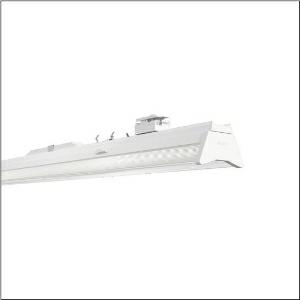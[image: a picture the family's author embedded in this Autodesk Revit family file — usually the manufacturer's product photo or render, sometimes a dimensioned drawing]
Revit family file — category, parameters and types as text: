
# Revit family: licross_r__11_performance_ho_51td16dn4fxm_21ba
name_source: partatom
category: Lighting Fixtures
units: mm (PartAtom-declared; Revit-internal decimal feet)

## family parameters
Cut with Voids When Loaded = No
Host = Face
Light Source = No
Part Type = Normal
Room Calculation Point = No
Round Connector Dimension = Use Diameter
Shared = No

## types (1)
- --- (1 x LED, 15460 lm, 87.3 W, 4000K)
    Apparent Load = 87 VA
    CIE Flux Codes = 63 87 95 78 100
    Color Rendering = 80
    Color Temperature = 4000K
    Default Elevation = 1800 mm
    Description = Licross® 11 Performance HO, luminaire insert, of sheet steel, galvanised, coil coated, white, length: 1.500mm, width: 120mm, height: 123mm, LED rated luminous flux: 15.460lm, light colour: 840, control gear: DALI 2, with plug, 5-pole, with phase selection, mains connection: 220..240V, AC, 50/60Hz, rated input power: 87W, internal wiring halogen-free, primary light control with lens, of plastic, primary optical cover: cover, of PMMA, light emission: direct/indirect distribution, primary light characteristic: symmetric, protection rating (complete): IP54, insulation class (complete): insulation class I (protective earthing), certification: CE, ENEC, VDE, UKCA, protection symbol: D if used in an environment with non-conductive dust loads with corresponding accessories, impact resistance: IK06, permissible ambient temperature for indoor applications: -25..+30°C, corresponds to IFS (International Featured Standards) requirements for safety and quality in the food industry, reducing of maximum allowable ambient temperature of 5°C with ceiling mounting, LABS conformity tested according to VDMA 24364:2018-05, packaging unit: 1 piece
    Height = 114 mm
    Lamp = 1 x LED
    Lamp Light Flux = 15460 lm
    Lamp Power = 87.3 W
    Lamp count = 1
    Length = 1500 mm
    Luminous efficacy = 177 lm/W
    Manufacturer = Siteco
    ModVariant = No
    Model = 51TD16DN4FXM
    Mounting Place = Ceiling
    Mounting Type = Pendant
    Number of Poles = 1
    OnlyDefault = Yes
    Power Factor = 1
    Product Name = Licross® 11 Performance HO
    Product group = luminaire insert | ceiling pendant
    ProductGroupID = 902
    Protection Class = Protection class I
    Protection Degree = IP 54
    RLX_Detail_Level = 1
    RLX_Emergency_Light_Flux = 0 lm
    RLX_Emergency_Type = 0
    RLX_Emergency_Type_DB = No
    RlxData = <blob elided: 34065 chars, md5=6f273e90>
    Socket = socket
    Standby Power = 0 W
    System Light Flux = 15460 lm
    System Power = 87 W
    Type Comments = factory setting: luminous flux: 100 % | dim-lin: 254 | 589 mA
    Type Image = l_1256138.jpg
    URL = http://relux.com
    VarID = @adj_122785
    Voltage = 0 V
    Weight = 0.00 kg
    Width = 120 mm

## geometry (parser evidence)
native form markers: Blend x4, Sweep x12
no freeform markers — native parametric forms only
